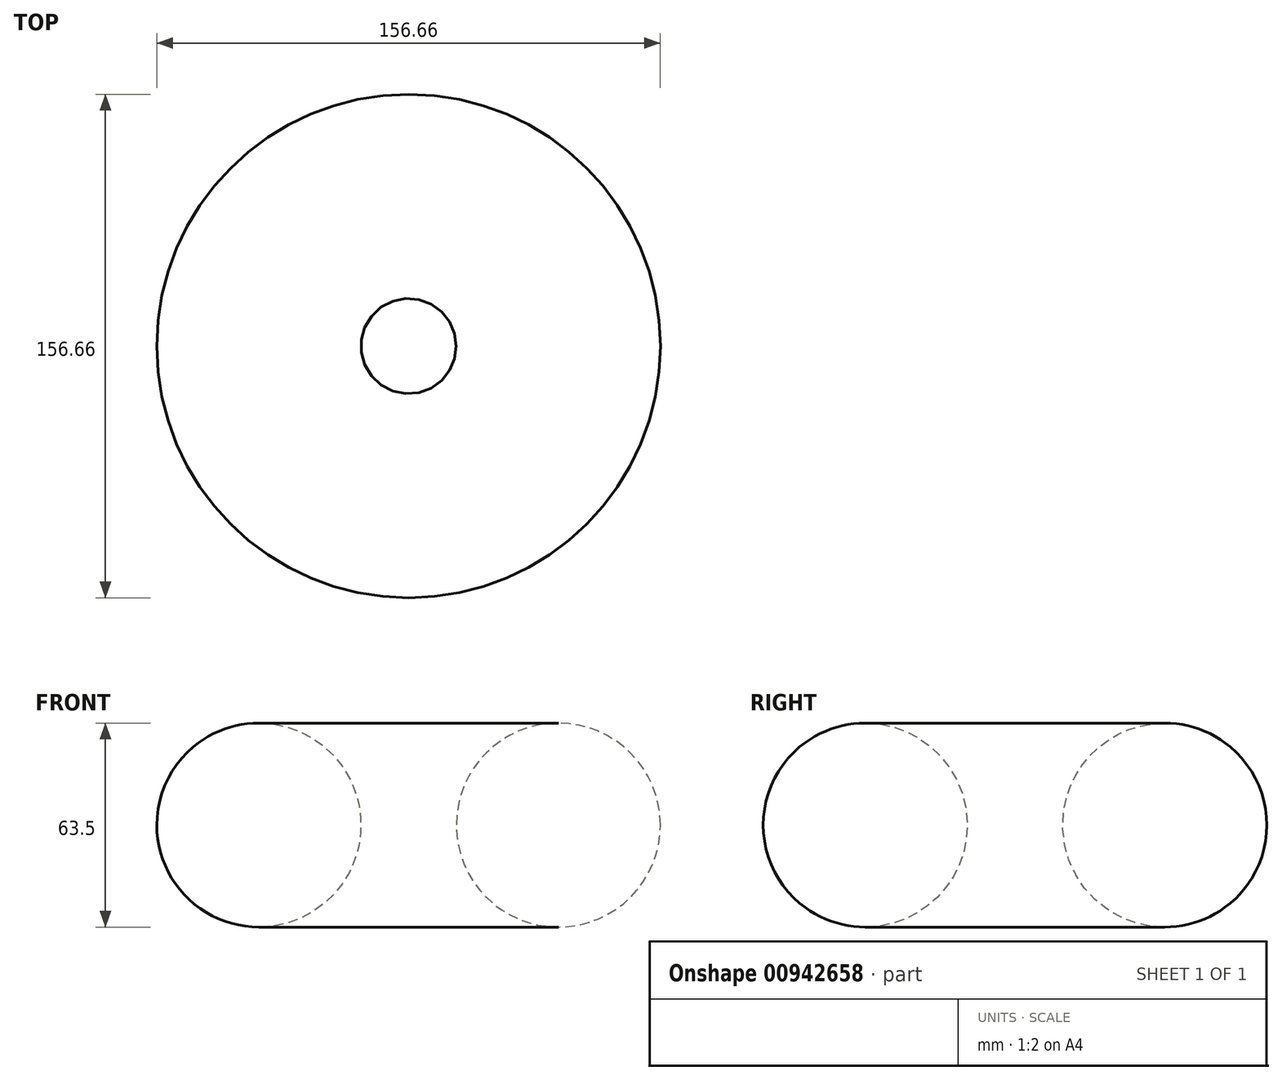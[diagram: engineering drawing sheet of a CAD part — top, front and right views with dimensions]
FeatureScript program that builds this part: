
annotation { "Feature Type Name" : "Feature", "Feature Type Description" : "" }
export const myFeature = defineFeature(function(context is Context, id is Id, definition is map)
    precondition{}
    {
        {
            var Q0;
            Q0=qCreatedBy(makeId("Right.planeOp"),FACE);
            var sketch = newSketch(context, id + "F0", { "sketchPlane" : qUnion([Q0])});
            skLineSegment(sketch, "E0", {"start": v(0, 61.81) * mm, "end": v(0, -47.88) * mm, "construction": true});
            skCircle(sketch, "E1", {"center": v(46.58, 0) * mm, "radius": 31.75 * mm});
            skSolve(sketch);
        }
        {
            var Q0;
            Q0=makeQuery(id+"F0.imprint","IMPRINT",FACE,{"disambiguationData":[TD([[makeQuery(id+"F0.imprint","IMPRINT",EDGE,{"derivedFrom":sQuery(id+"F0.wireOp",EDGE,"E1")}),1.0]])]});
            var Q1;
            Q1=sQuery(id+"F0.wireOp",EDGE,"E0");
            revolve(context, id + "F1", {"surfaceOperationType" : NewSurfaceOperationType.NEW, "entities" : qUnion([Q0]), "axis" : qUnion([Q1]), "revolveType" : RevolveType.FULL});
        }
    });
